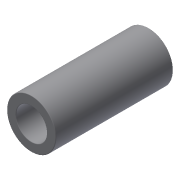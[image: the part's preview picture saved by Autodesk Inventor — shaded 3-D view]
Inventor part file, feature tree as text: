
AUTODESK INVENTOR PART (.ipt)
format: ipt  version: 2013 (Build 170138000, 138)  size: 103,424 bytes
history: native  units: in
note: dims shown in document units (in); Inventor stores cm internally (conversion verified against a paired STEP export)
features: fillet x1, other x1, imported_body x1
ambient origin geometry x8: Origin, YZ Plane, XZ Plane, XY Plane, X Axis, Y Axis, Z Axis, Center Point
feature tree (3):
  fillet  "Fillet1"  [1 undecoded]
  other  "2x500 Spacer1"
  imported_body  "Base1"
note: 1 required parameter value undecoded (feature->parameter linkage not recoverable at this tier; creation-order binding heuristic only, values carry confidence <= 0.55)
